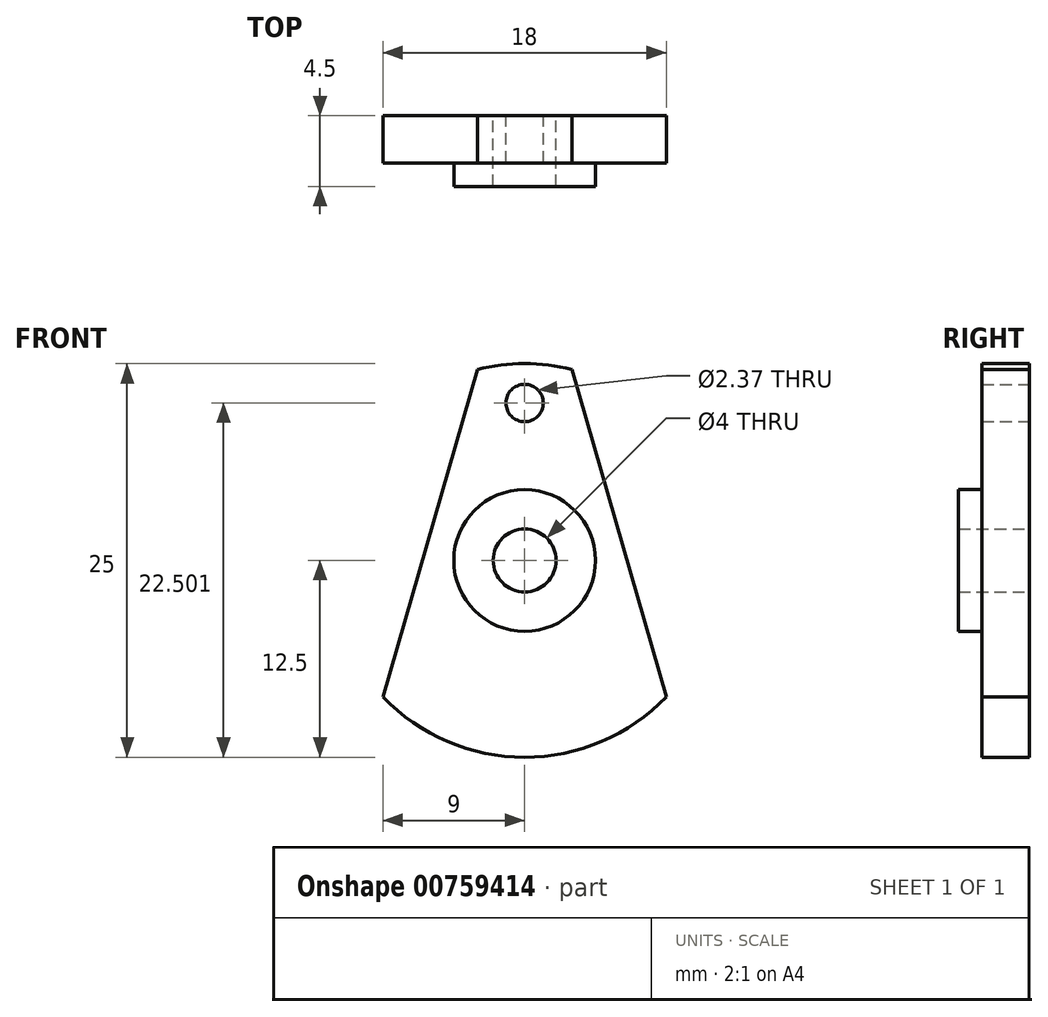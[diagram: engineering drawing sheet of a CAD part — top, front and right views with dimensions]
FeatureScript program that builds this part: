
annotation { "Feature Type Name" : "Feature", "Feature Type Description" : "" }
export const myFeature = defineFeature(function(context is Context, id is Id, definition is map)
    precondition{}
    {
        {
            var Q0;
            Q0=qCreatedBy(makeId("Front.planeOp"),FACE);
            var sketch = newSketch(context, id + "F0", { "sketchPlane" : qUnion([Q0])});
            skCircle(sketch, "E0", {"center": v(0, 0) * mm, "radius": 4.5 * mm});
            skArc(sketch, "E1", {"start": v(3, 12.13) * mm, "mid": v(0, 12.5) * mm, "end": v(-3, 12.13) * mm});
            skLineSegment(sketch, "E2", {"start": v(3, 12.13) * mm, "end": v(9, -8.67) * mm});
            skLineSegment(sketch, "E3.MirrorCS", {"start": v(-3, 12.13) * mm, "end": v(-9, -8.67) * mm});
            skArc(sketch, "E4.trimOffspring", {"start": v(-9, -8.67) * mm, "mid": v(0, -12.5) * mm, "end": v(9, -8.67) * mm});
            skCircle(sketch, "E5", {"center": v(0, 0) * mm, "radius": 2 * mm});
            skCircle(sketch, "E6", {"center": v(0, 10) * mm, "radius": 1.19 * mm});
            skSolve(sketch);
        }
        {
            var Q0;
            Q0=makeQuery(id+"F0.imprint","IMPRINT",FACE,{"disambiguationData":[TD([[makeQuery(id+"F0.imprint","IMPRINT",EDGE,{"derivedFrom":sQuery(id+"F0.wireOp",EDGE,"E0")}),-1.0]])]});
            var Q1;
            Q1=makeQuery(id+"F0.imprint","IMPRINT",FACE,{"disambiguationData":[TD([[makeQuery(id+"F0.imprint","IMPRINT",EDGE,{"derivedFrom":sQuery(id+"F0.wireOp",EDGE,"E0")}),1.0]])]});
            extrude(context, id + "F1", {"entities" : qUnion([Q0, Q1]), "depth" : 3 * mm, "offsetDistance" : 25 * mm});
        }
        {
            var Q0;
            Q0=makeQuery(id+"F0.imprint","IMPRINT",FACE,{"disambiguationData":[TD([[makeQuery(id+"F0.imprint","IMPRINT",EDGE,{"derivedFrom":sQuery(id+"F0.wireOp",EDGE,"E0")}),1.0]])]});
            extrude(context, id + "F2", {"entities" : qUnion([Q0]), "operationType" : NewBodyOperationType.ADD, "depth" : 4.5 * mm, "offsetDistance" : 25 * mm});
        }
    });
